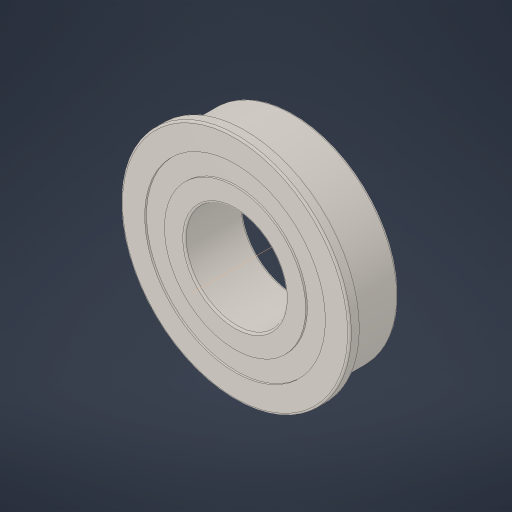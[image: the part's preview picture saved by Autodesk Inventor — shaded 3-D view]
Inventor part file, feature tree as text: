
AUTODESK INVENTOR PART (.ipt)
format: ipt  version: 2023.3 (Build 273359000, 359)  size: 279,040 bytes
history: native  units: in
note: dims shown in document units (in); Inventor stores cm internally (conversion verified against a paired STEP export)
features: other x1, revolve x1, sketch x1, fillet x1
ambient origin geometry x8: Origin, YZ Plane, XZ Plane, XY Plane, X Axis, Y Axis, Z Axis, Center Point
bodies: Solid1 (feature_tree)
feature tree (4):
  other  "Work Axis1"
  revolve  "Revolution1"  [1 undecoded]
  sketch  "Sketch1"  dims[d0=90.0deg]
  fillet  "Fillet1"  [1 undecoded]
note: 2 required parameter values undecoded (feature->parameter linkage not recoverable at this tier; creation-order binding heuristic only, values carry confidence <= 0.55)
